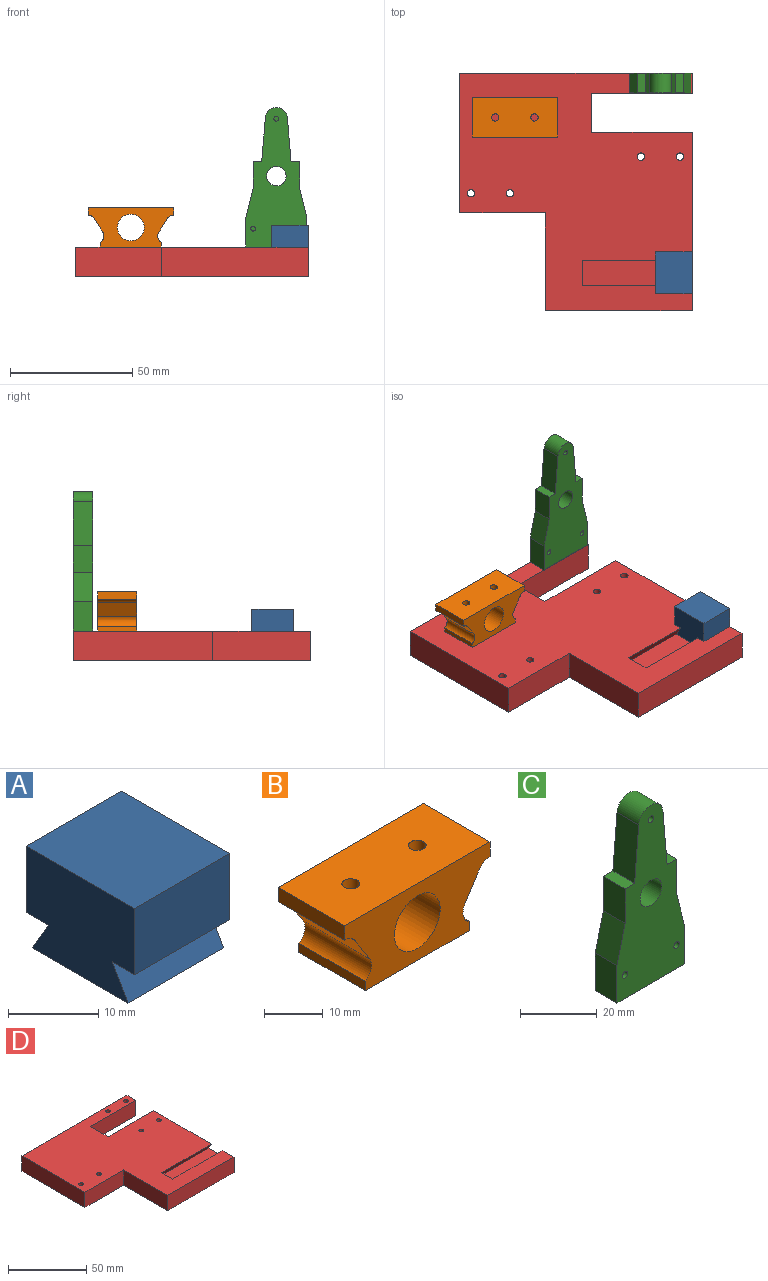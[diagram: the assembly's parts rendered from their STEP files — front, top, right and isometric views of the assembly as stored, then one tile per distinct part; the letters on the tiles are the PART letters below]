
ASSEMBLY  parts=4 mates=3
PART A: 10 faces, bbox 15x17x13.3 mm
  f0: plane 15x9mm, normal (0,1,0), area 135mm2, adj f1,f7,f8,f9
  f1: plane 17x15mm, normal (0,0,1), area 255mm2, adj f0,f2,f8,f9
  f2: plane 15x9mm, normal (0,-1,0), area 135mm2, adj f1,f3,f8,f9
  f3: plane 15x3.5mm, normal (0,0,-1), area 52.5mm2, adj f2,f4,f8,f9
  f4: plane 15x4.33mm, normal (0,-0.87,0.5), area 75mm2, adj f3,f5,f8,f9
  f5: plane 15x15mm, normal (0,0,-1), area 225mm2, adj f4,f6,f8,f9
  f6: plane 15x4.33mm, normal (0,0.87,0.5), area 75mm2, adj f5,f7,f8,f9
  f7: plane 15x3.5mm, normal (0,0,-1), area 52.5mm2, adj f0,f6,f8,f9
  f8: plane 17x13.33mm, normal (1,0,0), area 207.1mm2, adj f0,f1,f2,f3,f4,f5,f6,f7
  f9: plane 17x13.33mm, normal (-1,0,0), area 207.1mm2, adj f0,f1,f2,f3,f4,f5,f6,f7
PART B: 17 faces, bbox 35x16x16 mm
  f0: plane 25x16mm, normal (0,0,-1), area 385.9mm2, adj f2,f3,f13,f14,f15,f16
  f1: plane 35x16mm, normal (0,0,1), area 545.9mm2, adj f7,f8,f13,f14,f15,f16
  f2: plane 16x1.9mm, normal (-1,0,0), area 30.4mm2, adj f0,f11,f13,f14
  f3: plane 16x1.9mm, normal (1,0,0), area 30.4mm2, adj f0,f4,f13,f14
  f4: cylinder r=3mm len=16mm, axis (0,-1,0), area 77.5mm2, adj f3,f5,f13,f14
  f5: plane 16x5.5mm, normal (0.84,0,-0.54), area 104.3mm2, adj f4,f6,f13,f14
  f6: cylinder r=3mm len=16mm, axis (0,-1,0), area 48.2mm2, adj f5,f7,f13,f14
  f7: plane 16x3mm, normal (1,0,0), area 48mm2, adj f1,f6,f13,f14
  f8: plane 16x3mm, normal (-1,0,0), area 48mm2, adj f1,f9,f13,f14
  f9: cylinder r=3mm len=16mm, axis (0,-1,0), area 48.2mm2, adj f8,f10,f13,f14
  f10: plane 16x5.5mm, normal (-0.84,0,-0.54), area 104.3mm2, adj f9,f11,f13,f14
  f11: cylinder r=3mm len=16mm, axis (0,-1,0), area 77.5mm2, adj f2,f10,f13,f14
  f12: cylinder r=5.5mm len=16mm, axis (0,-1,0), area 552.9mm2, adj f13,f14
  f13: plane 35x16mm, normal (0,1,0), area 341.9mm2, adj f0,f1,f2,f3,f4,f5,f6,f7
  f14: plane 35x16mm, normal (0,-1,0), area 341.9mm2, adj f0,f1,f2,f3,f4,f5,f6,f7
  f15: cylinder r=1.5mm len=16mm, axis (0,0,-1), area 150.8mm2, adj f0,f1
  f16: cylinder r=1.5mm len=16mm, axis (0,0,-1), area 150.8mm2, adj f0,f1
PART C: 25 faces, bbox 25x8x57 mm
  f0: plane 25x8mm, normal (0,0,-1), area 185.9mm2, adj f1,f11,f12,f14,f21,f23
  f1: plane 57x25mm, normal (0,-1,0), area 929.2mm2, adj f0,f2,f3,f4,f5,f6,f7,f8
  f2: plane 12x8mm, normal (-0.97,0,0.24), area 99mm2, adj f1,f3,f12,f14
  f3: plane 11x8mm, normal (-1,0,0), area 88mm2, adj f1,f2,f4,f14
  f4: plane 8x3.5mm, normal (0,0,1), area 28mm2, adj f1,f3,f5,f14
  f5: plane 17.88x8mm, normal (-1,0,0.08), area 143.6mm2, adj f1,f4,f6,f14
  f6: cylinder r=4.5mm len=8.97mm, axis (0,-1,0), area 107mm2, adj f1,f5,f7,f14
  f7: plane 17.88x8mm, normal (1,0,0.08), area 143.6mm2, adj f1,f6,f8,f14
  f8: plane 8x3.5mm, normal (0,0,1), area 28mm2, adj f1,f7,f9,f14
  f9: plane 11x8mm, normal (1,0,0), area 88mm2, adj f1,f8,f10,f14
  f10: plane 12x8mm, normal (0.97,0,0.24), area 99mm2, adj f1,f9,f11,f14
  f11: plane 12x8mm, normal (1,0,0), area 96mm2, adj f0,f1,f10,f14
  f12: plane 12x8mm, normal (-1,0,0), area 96mm2, adj f0,f1,f2,f14
  f13: cylinder r=4mm len=8mm, axis (0,-1,0), area 201.1mm2, adj f1,f14
  f14: plane 57x25mm, normal (0,1,0), area 938.6mm2, adj f0,f2,f3,f4,f5,f6,f7,f8
  f15: cylinder r=1mm len=5mm, axis (0,-1,0), area 31.4mm2, adj f1,f16
  f16: plane 2x2mm, normal (0,-1,0), area 3.1mm2, adj f15
  f17: cylinder r=1mm len=5mm, axis (0,-1,0), area 31.4mm2, adj f1,f18
  f18: plane 2x2mm, normal (0,-1,0), area 3.1mm2, adj f17
  f19: cylinder r=1mm len=5mm, axis (0,-1,0), area 31.4mm2, adj f1,f20
  f20: plane 2x2mm, normal (0,-1,0), area 3.1mm2, adj f19
  f21: cylinder r=1.5mm len=6mm, axis (0,0,-1), area 56.5mm2, adj f0,f22
  f22: plane 3x3mm, normal (0,0,-1), area 7.1mm2, adj f21
  f23: cylinder r=1.5mm len=6mm, axis (0,0,-1), area 56.5mm2, adj f0,f24
  f24: plane 3x3mm, normal (0,0,-1), area 7.1mm2, adj f23
PART D: 22 faces, bbox 95x97x12 mm
  f0: plane 97x95mm, normal (0,0,1), area 6666.6mm2, adj f1,f2,f4,f5,f6,f7,f8,f9
  f1: plane 73x12mm, normal (1,0,0), area 821.9mm2, adj f0,f3,f5,f16,f18,f19,f20
  f2: plane 35x12mm, normal (0,-1,0), area 420mm2, adj f0,f3,f4,f17
  f3: plane 97x95mm, normal (0,0,-1), area 7116.6mm2, adj f1,f2,f4,f5,f6,f7,f8,f9
  f4: plane 57x12mm, normal (-1,0,0), area 684mm2, adj f0,f2,f3,f9
  f5: plane 41x12mm, normal (0,1,0), area 492mm2, adj f0,f1,f3,f6
  f6: plane 16x12mm, normal (1,0,0), area 192mm2, adj f0,f3,f5,f7
  f7: plane 41x12mm, normal (0,-1,0), area 492mm2, adj f0,f3,f6,f8
  f8: plane 12x8mm, normal (1,0,0), area 96mm2, adj f0,f3,f7,f9
  f9: plane 95x12mm, normal (0,1,0), area 1140mm2, adj f0,f3,f4,f8
  f10: cylinder r=1.5mm len=12mm, axis (0,0,-1), area 113.1mm2, adj f0,f3
  f11: cylinder r=1.5mm len=12mm, axis (0,0,-1), area 113.1mm2, adj f0,f3
  f12: cylinder r=1.5mm len=12mm, axis (0,0,-1), area 113.1mm2, adj f0,f3
  f13: cylinder r=1.5mm len=12mm, axis (0,0,-1), area 113.1mm2, adj f0,f3
  f14: cylinder r=1.5mm len=12mm, axis (0,0,-1), area 113.1mm2, adj f0,f3
  f15: cylinder r=1.5mm len=12mm, axis (0,0,-1), area 113.1mm2, adj f0,f3
  f16: plane 60x12mm, normal (0,-1,0), area 720mm2, adj f0,f1,f3,f17
  f17: plane 40x12mm, normal (-1,0,0), area 480mm2, adj f0,f2,f3,f16
  f18: plane 45x15mm, normal (0,0,1), area 675mm2, adj f1,f19,f20,f21
  f19: plane 45x4.33mm, normal (0,-0.87,-0.5), area 225mm2, adj f0,f1,f18,f21
  f20: plane 45x4.33mm, normal (0,0.87,-0.5), area 225mm2, adj f0,f1,f18,f21
  f21: plane 15x4.33mm, normal (1,0,0), area 54.1mm2, adj f0,f18,f19,f20
PLACE A t=(-7.84,9.87,-10.29)mm
PLACE B t=(17.16,40.87,-10.29)mm
PLACE C t=(7.16,39.87,-10.29)mm
PLACE D t=(7.16,9.87,-10.29)mm fixed
MATE fastened D.f0 <-> B.f0  axis (0,0,1) through (7.16,66.87,1.71)mm
MATE slider A.f8 <-> D.f1  axis (-1,0,0) through (102.16,-22.13,-2.62)mm
MATE fastened C.f23 <-> D.f12  axis (0,0,-1) through (81.16,62.87,1.71)mm
